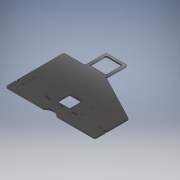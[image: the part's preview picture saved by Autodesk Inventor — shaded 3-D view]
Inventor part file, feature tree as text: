
AUTODESK INVENTOR PART (.ipt)
format: ipt  version: 2018 (Build 220112000, 112)  size: 234,496 bytes
history: native  units: mm
features: extrude x2, sketch x2, other x1, fillet x1
ambient origin geometry x8: Origin, YZ Plane, XZ Plane, XY Plane, X Axis, Y Axis, Z Axis, Center Point
bodies: Body1 (feature_tree)
feature tree (6):
  other  "Sólido1"
  extrude  "Extrusión1"  Depth=95.0mm
  fillet  "Empalme1"  Radius=95.0mm
  extrude  "Extrusión2"  Depth=400.0mm
  sketch  "Boceto1"  dims[d2=260.0mm d3=95.0mm d4=95.0mm]
  sketch  "Boceto2"  dims[d5=150.0mm d6=400.0mm d7=57.0mm d8=57.0mm d10=75.0mm d11=75.0mm d12=6.0mm d13=0.0mm d14=6.0mm d15=20.0mm d16=6.0mm d17=48.0mm d18=20.0mm d19=60.0mm d20=20.0mm d21=60.0mm d22=8.0mm d23=20.0mm d24=6.0mm d25=110.0mm d26=6.0mm d27=20.0mm d28=12.0mm d29=6.0mm d30=44.0mm d31=6.0mm d32=6.0mm d33=40.0mm d34=3.0mm d35=0.0mm d36=6.0mm d37=6.0mm]
